annotation { "Feature Type Name" : "Feature", "Feature Type Description" : "" }
export const myFeature = defineFeature(function(context is Context, id is Id, definition is map)
    precondition{}
    {
        {
            var Q0;
            Q0=qCreatedBy(makeId("Top.planeOp"),FACE);
            var sketch = newSketch(context, id + "F0", { "sketchPlane" : qUnion([Q0])});
            skLineSegment(sketch, "E0.bottom", {"start": v(63.5, 38.1) * mm, "end": v(-63.5, 38.1) * mm});
            skLineSegment(sketch, "E0.top", {"start": v(63.5, -50.8) * mm, "end": v(-63.5, -50.8) * mm});
            skLineSegment(sketch, "E0.left", {"start": v(63.5, 38.1) * mm, "end": v(63.5, -50.8) * mm});
            skLineSegment(sketch, "E0.right", {"start": v(-63.5, 38.1) * mm, "end": v(-63.5, -50.8) * mm});
            skPoint(sketch, "E0.middle", {"position": v(0, -6.35) * mm});
            skText(sketch, "E1", { "text": "Brandon Ortega", "fontName": "OpenSans-Regular.ttf"});
            skLineSegment(sketch, "E2.bottom", {"start": v(69.85, 44.45) * mm, "end": v(-69.85, 44.45) * mm});
            skLineSegment(sketch, "E2.top", {"start": v(69.85, -57.15) * mm, "end": v(-69.85, -57.15) * mm});
            skLineSegment(sketch, "E2.left", {"start": v(69.85, 44.45) * mm, "end": v(69.85, -57.15) * mm});
            skLineSegment(sketch, "E2.right", {"start": v(-69.85, 44.45) * mm, "end": v(-69.85, -57.15) * mm});
            skLineSegment(sketch, "E3", {"start": v(-69.85, -15.2) * mm, "end": v(58.84, -15.2) * mm});
            skLineSegment(sketch, "E4", {"start": v(-14.4, -11.23) * mm, "end": v(-14.4, -9.9) * mm});
            skLineSegment(sketch, "E5", {"start": v(-14.4, -9.9) * mm, "end": v(-10.98, -8.24) * mm});
            skLineSegment(sketch, "E6", {"start": v(-10.98, -8.24) * mm, "end": v(-7.17, -8.24) * mm});
            skLineSegment(sketch, "E7", {"start": v(-7.17, -8.24) * mm, "end": v(-7.17, -6.75) * mm});
            skLineSegment(sketch, "E8", {"start": v(-7.17, -6.75) * mm, "end": v(-3.36, -6.75) * mm});
            skLineSegment(sketch, "E9", {"start": v(-3.36, -6.75) * mm, "end": v(3.92, -9) * mm});
            skFitSpline(sketch, "E10", {"points": [v(3.92, -9) * mm, v(6, -9.48) * mm, v(8.35, -9.23) * mm], "startDerivative": vector(4.23, -1.18) * mm, "endDerivative": vector(5.03, -0.02) * mm});
            skLineSegment(sketch, "E11", {"start": v(34.66, -10.89) * mm, "end": v(53.71, -10.89) * mm});
            skLineSegment(sketch, "E12", {"start": v(53.71, -10.89) * mm, "end": v(54.3, -11.57) * mm});
            skLineSegment(sketch, "E13", {"start": v(54.3, -11.57) * mm, "end": v(54.3, -13.42) * mm});
            skLineSegment(sketch, "E14", {"start": v(54.3, -13.42) * mm, "end": v(58.84, -13.42) * mm});
            skLineSegment(sketch, "E15", {"start": v(58.84, -13.42) * mm, "end": v(58.84, -15.2) * mm});
            skLineSegment(sketch, "E16.MirrorCS", {"start": v(58.84, -17) * mm, "end": v(58.84, -15.2) * mm});
            skLineSegment(sketch, "E17.MirrorCS", {"start": v(54.3, -17) * mm, "end": v(58.84, -17) * mm});
            skLineSegment(sketch, "E18.MirrorCS", {"start": v(54.3, -18.85) * mm, "end": v(54.3, -17) * mm});
            skLineSegment(sketch, "E19.MirrorCS", {"start": v(53.71, -19.53) * mm, "end": v(54.3, -18.85) * mm});
            skLineSegment(sketch, "E20.MirrorCS", {"start": v(34.66, -19.53) * mm, "end": v(53.71, -19.53) * mm});
            skFitSpline(sketch, "E21.MirrorCS", {"points": [v(3.92, -21.41) * mm, v(6, -20.94) * mm, v(8.35, -21.19) * mm], "startDerivative": vector(4.23, 1.18) * mm, "endDerivative": vector(5.03, 0.02) * mm});
            skLineSegment(sketch, "E22.MirrorCS", {"start": v(-3.36, -23.67) * mm, "end": v(3.92, -21.41) * mm});
            skLineSegment(sketch, "E23.MirrorCS", {"start": v(-7.17, -23.67) * mm, "end": v(-3.36, -23.67) * mm});
            skLineSegment(sketch, "E24.MirrorCS", {"start": v(-7.17, -22.18) * mm, "end": v(-7.17, -23.67) * mm});
            skLineSegment(sketch, "E25.MirrorCS", {"start": v(-10.98, -22.18) * mm, "end": v(-7.17, -22.18) * mm});
            skLineSegment(sketch, "E26.MirrorCS", {"start": v(-14.4, -20.52) * mm, "end": v(-10.98, -22.18) * mm});
            skLineSegment(sketch, "E27.MirrorCS", {"start": v(-14.4, -19.2) * mm, "end": v(-14.4, -20.52) * mm});
            skLineSegment(sketch, "E28", {"start": v(3.92, -8.76) * mm, "end": v(3.92, -9) * mm});
            skLineSegment(sketch, "E29", {"start": v(33.75, -9.23) * mm, "end": v(34.66, -10.89) * mm});
            skLineSegment(sketch, "E30", {"start": v(33.75, -21.19) * mm, "end": v(34.66, -19.53) * mm});
            skLineSegment(sketch, "E31.MirrorCS", {"start": v(3.92, -21.66) * mm, "end": v(3.92, -21.41) * mm});
            skLineSegment(sketch, "E32", {"start": v(-14.4, -11.23) * mm, "end": v(-22.17, -11.23) * mm});
            skLineSegment(sketch, "E33", {"start": v(-14.4, -19.2) * mm, "end": v(-22.17, -19.2) * mm});
            skLineSegment(sketch, "E34", {"start": v(8.35, -9.23) * mm, "end": v(33.75, -9.23) * mm});
            skLineSegment(sketch, "E35", {"start": v(8.35, -21.19) * mm, "end": v(33.75, -21.19) * mm});
            skLineSegment(sketch, "E36", {"start": v(-22.17, -11.23) * mm, "end": v(-37.76, -9.23) * mm});
            skLineSegment(sketch, "E37", {"start": v(-37.76, -9.23) * mm, "end": v(-37.76, -11.23) * mm});
            skLineSegment(sketch, "E38.MirrorCS", {"start": v(-22.17, -19.2) * mm, "end": v(-37.76, -21.19) * mm});
            skLineSegment(sketch, "E39.MirrorCS", {"start": v(-37.76, -21.19) * mm, "end": v(-37.76, -19.2) * mm});
            skLineSegment(sketch, "E40", {"start": v(-37.76, -11.23) * mm, "end": v(-44.14, -11.23) * mm});
            skLineSegment(sketch, "E41", {"start": v(-44.14, -11.23) * mm, "end": v(-55.78, -15.2) * mm});
            skLineSegment(sketch, "E42.MirrorCS", {"start": v(-37.76, -19.2) * mm, "end": v(-44.14, -19.2) * mm});
            skLineSegment(sketch, "E43.MirrorCS", {"start": v(-44.14, -19.2) * mm, "end": v(-55.78, -15.2) * mm});
            skPoint(sketch, "E44.4.internal.snap0", {"position": v(58.84, -14.31) * mm});
            skFitSpline(sketch, "E44", {"points": [v(58.84, -14.31) * mm, v(60.9, -14.92) * mm, v(62.3, -18) * mm, v(60.68, -21.52) * mm, v(58.84, -29.26) * mm, v(57.67, -36.4) * mm, v(51.53, -40.22) * mm, v(44.5, -35.6) * mm, v(35.05, -31.67) * mm, v(26.4, -33.2) * mm, v(18.56, -39.62) * mm, v(6.99, -38.02) * mm, v(-3.16, -33.39) * mm, v(-22.92, -39.26) * mm, v(-30.57, -37.84) * mm], "startDerivative": vector(58.2, -4.08) * mm, "endDerivative": vector(-91.94, 42.35) * mm});
            skFitSpline(sketch, "E45", {"points": [v(58.84, -16.1) * mm, v(59.89, -16.53) * mm, v(60.16, -18.23) * mm, v(58.41, -20.86) * mm, v(56.94, -27.67) * mm, v(55.95, -34.6) * mm, v(52.73, -37.5) * mm, v(45.96, -34.12) * mm, v(37.19, -29.93) * mm, v(29.37, -29.93) * mm, v(22.29, -33.31) * mm, v(18.34, -36.7) * mm, v(14.16, -37.66) * mm, v(3.83, -33.39) * mm, v(-3.16, -30.04) * mm, v(-13.35, -31.9) * mm, v(-21.1, -34.81) * mm, v(-25.38, -36.2) * mm, v(-28.95, -35.05) * mm], "startDerivative": vector(48.19, -7.9) * mm, "endDerivative": vector(-79.65, 38.82) * mm});
            skLineSegment(sketch, "E46", {"start": v(-28.95, -35.05) * mm, "end": v(-30.57, -37.84) * mm});
            const initialGuessF0  = {"E1": [-0.05958, 0.00762, 1, 0, 0.01143]};
            skSetInitialGuess(sketch, initialGuessF0);
            skSolve(sketch);
        }
        {
            var Q0;
            Q0=makeQuery(id+"F0.imprint","IMPRINT",FACE,{"disambiguationData":[TD([[makeQuery(id+"F0.imprint","IMPRINT",EDGE,{"derivedFrom":sQuery(id+"F0.wireOp",EDGE,"E4")}),-1.0]])]});
            var Q1;
            Q1=sQuery(id+"F0.wireOp",EDGE,"E3");
            revolve(context, id + "F1", {"surfaceOperationType" : NewSurfaceOperationType.NEW, "entities" : qUnion([Q0]), "axis" : qUnion([Q1]), "revolveType" : RevolveType.ONE_DIRECTION, "angle" : 180 * degree});
        }
        {
            var Q0;
            {var subQ1=sQuery(id+"F0.wireOp",EDGE,"E44");Q0=makeQuery(id+"F0.imprint","IMPRINT",FACE,{"disambiguationData":[TD([[makeQuery(id+"F0.imprint","IMPRINT",EDGE,{"derivedFrom":subQ1}),-1.0]])]});}
            extrude(context, id + "F2", {"entities" : qUnion([Q0]), "operationType" : NewBodyOperationType.ADD, "depth" : 2.54 * mm, "offsetDistance" : 25.4 * mm});
        }
        {
            var Q0;
            Q0=makeQuery(id+"F2.opExtrude","CAP_EDGE",EDGE,{"disambiguationData":[OSD([sQuery(id+"F0.wireOp",EDGE,"E45")])],"isStart":false});
            fillet(context, id + "F3", {"entities" : qUnion([Q0]), "radius" : 0.5 * mm, "tangentPropagation" : true, "allowEdgeOverflow" : false});
        }
        {
            var Q0;
            Q0=makeQuery(id+"F2.opExtrude","CAP_EDGE",EDGE,{"disambiguationData":[OSD([sQuery(id+"F0.wireOp",EDGE,"E44")])],"isStart":false});
            fillet(context, id + "F4", {"entities" : qUnion([Q0]), "radius" : 0.5 * mm, "tangentPropagation" : true, "allowEdgeOverflow" : false});
        }
        {
            var Q0;
            {var subQ8=sQuery(id+"F0.wireOp",EDGE,"E1.sketch_text.stroke-3");Q0=makeQuery(id+"F0.imprint","IMPRINT",FACE,{"disambiguationData":[TD([[makeQuery(id+"F0.imprint","IMPRINT",EDGE,{"derivedFrom":subQ8}),-1.0]])]});}
            var Q1;
            {var subQ2=sQuery(id+"F0.wireOp",EDGE,"E1.sketch_text.stroke-0");Q1=makeQuery(id+"F0.imprint","IMPRINT",FACE,{"disambiguationData":[TD([[makeQuery(id+"F0.imprint","IMPRINT",EDGE,{"derivedFrom":subQ2}),-1.0]])]});}
            var Q2;
            Q2=makeQuery(id+"F0.imprint","IMPRINT",FACE,{"disambiguationData":[TD([[makeQuery(id+"F0.imprint","IMPRINT",EDGE,{"derivedFrom":sQuery(id+"F0.wireOp",EDGE,"E1.sketch_text.stroke-25")}),-1.0]])]});
            var Q3;
            Q3=makeQuery(id+"F0.imprint","IMPRINT",FACE,{"disambiguationData":[TD([[makeQuery(id+"F0.imprint","IMPRINT",EDGE,{"derivedFrom":sQuery(id+"F0.wireOp",EDGE,"E1.sketch_text.stroke-38")}),-1.0]])]});
            var Q4;
            Q4=makeQuery(id+"F0.imprint","IMPRINT",FACE,{"disambiguationData":[TD([[makeQuery(id+"F0.imprint","IMPRINT",EDGE,{"derivedFrom":sQuery(id+"F0.wireOp",EDGE,"E1.sketch_text.stroke-65")}),-1.0]])]});
            var Q5;
            Q5=makeQuery(id+"F0.imprint","IMPRINT",FACE,{"disambiguationData":[TD([[makeQuery(id+"F0.imprint","IMPRINT",EDGE,{"derivedFrom":sQuery(id+"F0.wireOp",EDGE,"E1.sketch_text.stroke-82")}),-1.0]])]});
            var Q6;
            Q6=makeQuery(id+"F0.imprint","IMPRINT",FACE,{"disambiguationData":[TD([[makeQuery(id+"F0.imprint","IMPRINT",EDGE,{"derivedFrom":sQuery(id+"F0.wireOp",EDGE,"E1.sketch_text.stroke-106")}),-1.0]])]});
            var Q7;
            Q7=makeQuery(id+"F0.imprint","IMPRINT",FACE,{"disambiguationData":[TD([[makeQuery(id+"F0.imprint","IMPRINT",EDGE,{"derivedFrom":sQuery(id+"F0.wireOp",EDGE,"E1.sketch_text.stroke-123")}),-1.0]])]});
            var Q8;
            {var subQ1=sQuery(id+"F0.wireOp",EDGE,"E1.sketch_text.stroke-140");Q8=makeQuery(id+"F0.imprint","IMPRINT",FACE,{"disambiguationData":[TD([[makeQuery(id+"F0.imprint","IMPRINT",EDGE,{"derivedFrom":subQ1}),-1.0]])]});}
            var Q9;
            {var subQ0=sQuery(id+"F0.wireOp",EDGE,"E1.sketch_text.stroke-145");Q9=makeQuery(id+"F0.imprint","IMPRINT",FACE,{"disambiguationData":[TD([[makeQuery(id+"F0.imprint","IMPRINT",EDGE,{"derivedFrom":subQ0}),-1.0]])]});}
            var Q10;
            Q10=makeQuery(id+"F0.imprint","IMPRINT",FACE,{"disambiguationData":[TD([[makeQuery(id+"F0.imprint","IMPRINT",EDGE,{"derivedFrom":sQuery(id+"F0.wireOp",EDGE,"E1.sketch_text.stroke-156")}),-1.0]])]});
            var Q11;
            Q11=makeQuery(id+"F0.imprint","IMPRINT",FACE,{"disambiguationData":[TD([[makeQuery(id+"F0.imprint","IMPRINT",EDGE,{"derivedFrom":sQuery(id+"F0.wireOp",EDGE,"E1.sketch_text.stroke-169")}),-1.0]])]});
            var Q12;
            {var subQ5=sQuery(id+"F0.wireOp",EDGE,"E1.sketch_text.stroke-180");Q12=makeQuery(id+"F0.imprint","IMPRINT",FACE,{"disambiguationData":[TD([[makeQuery(id+"F0.imprint","IMPRINT",EDGE,{"derivedFrom":subQ5}),-1.0]])]});}
            var Q13;
            Q13=makeQuery(id+"F0.imprint","IMPRINT",FACE,{"disambiguationData":[TD([[makeQuery(id+"F0.imprint","IMPRINT",EDGE,{"derivedFrom":sQuery(id+"F0.wireOp",EDGE,"E1.sketch_text.stroke-188")}),-1.0]])]});
            var Q14;
            Q14=makeQuery(id+"F0.imprint","IMPRINT",FACE,{"disambiguationData":[TD([[makeQuery(id+"F0.imprint","IMPRINT",EDGE,{"derivedFrom":sQuery(id+"F0.wireOp",EDGE,"E1.sketch_text.stroke-207")}),-1.0]])]});
            var Q15;
            Q15=makeQuery(id+"F0.imprint","IMPRINT",FACE,{"disambiguationData":[TD([[makeQuery(id+"F0.imprint","IMPRINT",EDGE,{"derivedFrom":sQuery(id+"F0.wireOp",EDGE,"E1.sketch_text.stroke-251")}),-1.0]])]});
            extrude(context, id + "F5", {"entities" : qUnion([Q0, Q1, Q2, Q3, Q4, Q5, Q6, Q7, Q8, Q9, Q10, Q11, Q12, Q13, Q14, Q15]), "depth" : 7.62 * mm, "offsetDistance" : 25.4 * mm});
        }
        {
            var Q0;
            {var subQ20=sQuery(id+"F0.wireOp",EDGE,"E0.top");Q0=makeQuery(id+"F0.imprint","IMPRINT",FACE,{"disambiguationData":[TD([[makeQuery(id+"F0.imprint","IMPRINT",EDGE,{"derivedFrom":subQ20}),-1.0]])]});}
            var Q1;
            Q1=makeQuery(id+"F0.imprint","IMPRINT",FACE,{"disambiguationData":[TD([[makeQuery(id+"F0.imprint","IMPRINT",EDGE,{"derivedFrom":sQuery(id+"F0.wireOp",EDGE,"E1.sketch_text.stroke-18")}),1.0]])]});
            var Q2;
            {var subQ5=sQuery(id+"F0.wireOp",EDGE,"E1.sketch_text.stroke-11");Q2=makeQuery(id+"F0.imprint","IMPRINT",FACE,{"disambiguationData":[TD([[makeQuery(id+"F0.imprint","IMPRINT",EDGE,{"derivedFrom":subQ5}),1.0]])]});}
            var Q3;
            Q3=makeQuery(id+"F0.imprint","IMPRINT",FACE,{"disambiguationData":[TD([[makeQuery(id+"F0.imprint","IMPRINT",EDGE,{"derivedFrom":sQuery(id+"F0.wireOp",EDGE,"E1.sketch_text.stroke-57")}),1.0]])]});
            var Q4;
            Q4=makeQuery(id+"F0.imprint","IMPRINT",FACE,{"disambiguationData":[TD([[makeQuery(id+"F0.imprint","IMPRINT",EDGE,{"derivedFrom":sQuery(id+"F0.wireOp",EDGE,"E1.sketch_text.stroke-97")}),1.0]])]});
            var Q5;
            Q5=makeQuery(id+"F0.imprint","IMPRINT",FACE,{"disambiguationData":[TD([[makeQuery(id+"F0.imprint","IMPRINT",EDGE,{"derivedFrom":sQuery(id+"F0.wireOp",EDGE,"E1.sketch_text.stroke-115")}),1.0]])]});
            var Q6;
            Q6=makeQuery(id+"F0.imprint","IMPRINT",FACE,{"disambiguationData":[TD([[makeQuery(id+"F0.imprint","IMPRINT",EDGE,{"derivedFrom":sQuery(id+"F0.wireOp",EDGE,"E1.sketch_text.stroke-148")}),1.0]])]});
            var Q7;
            Q7=makeQuery(id+"F0.imprint","IMPRINT",FACE,{"disambiguationData":[TD([[makeQuery(id+"F0.imprint","IMPRINT",EDGE,{"derivedFrom":sQuery(id+"F0.wireOp",EDGE,"E1.sketch_text.stroke-202")}),1.0]])]});
            var Q8;
            Q8=makeQuery(id+"F0.imprint","IMPRINT",FACE,{"disambiguationData":[TD([[makeQuery(id+"F0.imprint","IMPRINT",EDGE,{"derivedFrom":sQuery(id+"F0.wireOp",EDGE,"E1.sketch_text.stroke-245")}),1.0]])]});
            var Q9;
            Q9=makeQuery(id+"F0.imprint","IMPRINT",FACE,{"disambiguationData":[TD([[makeQuery(id+"F0.imprint","IMPRINT",EDGE,{"derivedFrom":sQuery(id+"F0.wireOp",EDGE,"E1.sketch_text.stroke-236")}),1.0]])]});
            var Q10;
            Q10=makeQuery(id+"F0.imprint","IMPRINT",FACE,{"disambiguationData":[TD([[makeQuery(id+"F0.imprint","IMPRINT",EDGE,{"derivedFrom":sQuery(id+"F0.wireOp",EDGE,"E1.sketch_text.stroke-270")}),1.0]])]});
            extrude(context, id + "F6", {"entities" : qUnion([Q0, Q1, Q2, Q3, Q4, Q5, Q6, Q7, Q8, Q9, Q10]), "depth" : 1.27 * mm, "offsetDistance" : 25.4 * mm});
        }
        {
            var Q0;
            {var subQ25=sQuery(id+"F0.wireOp",EDGE,"E0.top");Q0=makeQuery(id+"F0.imprint","IMPRINT",FACE,{"disambiguationData":[TD([[makeQuery(id+"F0.imprint","IMPRINT",EDGE,{"derivedFrom":subQ25}),1.0]])]});}
            extrude(context, id + "F7", {"entities" : qUnion([Q0]), "depth" : 10.16 * mm, "offsetDistance" : 25.4 * mm});
        }
    });